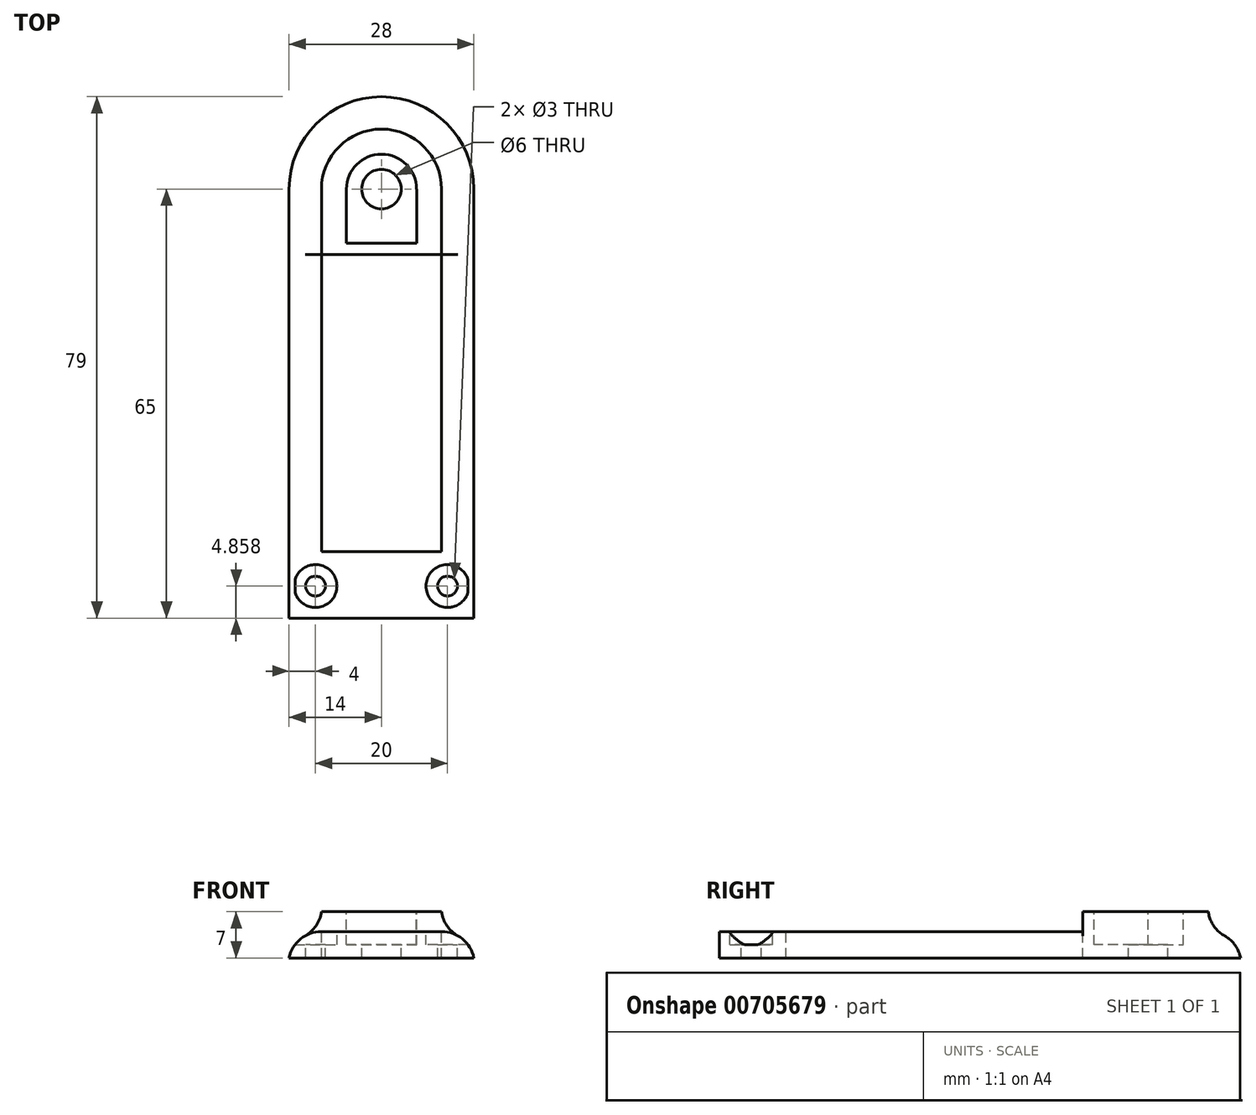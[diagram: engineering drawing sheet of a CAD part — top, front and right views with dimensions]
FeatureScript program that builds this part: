
annotation { "Feature Type Name" : "Feature", "Feature Type Description" : "" }
export const myFeature = defineFeature(function(context is Context, id is Id, definition is map)
    precondition{}
    {
        {
            var Q0;
            Q0=qCreatedBy(makeId("Top.planeOp"),FACE);
            var sketch = newSketch(context, id + "F0", { "sketchPlane" : qUnion([Q0])});
            skLineSegment(sketch, "E0.bottom", {"start": v(-14, 0) * mm, "end": v(14, 0) * mm});
            skLineSegment(sketch, "E0.top", {"start": v(-14, 65) * mm, "end": v(14, 65) * mm});
            skLineSegment(sketch, "E0.left", {"start": v(-14, 0) * mm, "end": v(-14, 65) * mm});
            skLineSegment(sketch, "E0.right", {"start": v(14, 0) * mm, "end": v(14, 65) * mm});
            skArc(sketch, "E1", {"start": v(14, 65) * mm, "mid": v(0, 79) * mm, "end": v(-14, 65) * mm});
            skSolve(sketch);
        }
        {
            var Q0;
            Q0=makeQuery(id+"F0.imprint","IMPRINT",FACE,{"disambiguationData":[TD([[makeQuery(id+"F0.imprint","IMPRINT",EDGE,{"derivedFrom":sQuery(id+"F0.wireOp",EDGE,"E0.bottom")}),1.0]])]});
            var Q1;
            Q1=makeQuery(id+"F0.imprint","IMPRINT",FACE,{"disambiguationData":[TD([[makeQuery(id+"F0.imprint","IMPRINT",EDGE,{"derivedFrom":sQuery(id+"F0.wireOp",EDGE,"E0.top")}),1.0]])]});
            extrude(context, id + "F1", {"entities" : qUnion([Q0, Q1]), "depth" : 4 * mm, "offsetDistance" : 25 * mm});
        }
        {
            var Q0;
            Q0=makeQuery(id+"F1.opExtrude","CAP_FACE",FACE,{"disambiguationData":[OSD([sQuery(id+"F0.wireOp",EDGE,"E0.bottom"),sQuery(id+"F0.wireOp",EDGE,"E0.left"),sQuery(id+"F0.wireOp",EDGE,"E0.right"),sQuery(id+"F0.wireOp",EDGE,"E1")])],"isStart":false});
            var sketch = newSketch(context, id + "F2", { "sketchPlane" : qUnion([Q0])});
            skCircle(sketch, "E2", {"center": v(-10, 4.86) * mm, "radius": 1.5 * mm});
            skSolve(sketch);
        }
        {
            var Q0;
            Q0=makeQuery(id+"F2.imprint","IMPRINT",FACE,{"disambiguationData":[TD([[makeQuery(id+"F2.imprint","IMPRINT",EDGE,{"derivedFrom":sQuery(id+"F2.wireOp",EDGE,"E2")}),1.0]])]});
            extrude(context, id + "F3", {"entities" : qUnion([Q0]), "operationType" : NewBodyOperationType.REMOVE, "oppositeDirection" : true, "depth" : 25 * mm, "offsetDistance" : 25 * mm});
        }
        {
            var Q0;
            Q0=makeQuery(id+"F1.opExtrude","CAP_FACE",FACE,{"disambiguationData":[OSD([sQuery(id+"F0.wireOp",EDGE,"E0.bottom"),sQuery(id+"F0.wireOp",EDGE,"E0.left"),sQuery(id+"F0.wireOp",EDGE,"E0.right"),sQuery(id+"F0.wireOp",EDGE,"E1")])],"isStart":false});
            var sketch = newSketch(context, id + "F4", { "sketchPlane" : qUnion([Q0])});
            skCircle(sketch, "E3", {"center": v(-10, 4.86) * mm, "radius": 3.25 * mm});
            skSolve(sketch);
        }
        {
            var Q0;
            Q0=makeQuery(id+"F4.imprint","IMPRINT",FACE,{"disambiguationData":[TD([[makeQuery(id+"F4.imprint","IMPRINT",EDGE,{"derivedFrom":sQuery(id+"F4.wireOp",EDGE,"E3")}),1.0]])]});
            extrude(context, id + "F5", {"entities" : qUnion([Q0]), "operationType" : NewBodyOperationType.REMOVE, "oppositeDirection" : true, "depth" : 2 * mm, "offsetDistance" : 25 * mm});
        }
        {
            var Q0;
            Q0=makeQuery(id+"F1.opExtrude","SWEPT_BODY",BODY,{"disambiguationData":[OSD([sQuery(id+"F0.wireOp",EDGE,"E0.bottom"),sQuery(id+"F0.wireOp",EDGE,"E0.left"),sQuery(id+"F0.wireOp",EDGE,"E0.right"),sQuery(id+"F0.wireOp",EDGE,"E1")])]});
            var Q1;
            Q1=qCreatedBy(makeId("Right.planeOp"),FACE);
            mirror(context, id + "F6", {"operationType" : NewBodyOperationType.INTERSECT, "entities" : qUnion([Q0]), "mirrorPlane" : qUnion([Q1])});
        }
        {
            var Q0;
            Q0=makeQuery(id+"F1.opExtrude","CAP_EDGE",EDGE,{"disambiguationData":[OSD([sQuery(id+"F0.wireOp",EDGE,"E0.left")])],"isStart":false});
            fillet(context, id + "F7", {"entities" : qUnion([Q0]), "radius" : 5 * mm, "tangentPropagation" : true, "allowEdgeOverflow" : false});
        }
        {
            var Q0;
            Q0=makeQuery(id+"F1.opExtrude","CAP_FACE",FACE,{"disambiguationData":[OSD([sQuery(id+"F0.wireOp",EDGE,"E0.bottom"),sQuery(id+"F0.wireOp",EDGE,"E0.left"),sQuery(id+"F0.wireOp",EDGE,"E0.right"),sQuery(id+"F0.wireOp",EDGE,"E1")])],"isStart":false});
            var sketch = newSketch(context, id + "F8", { "sketchPlane" : qUnion([Q0])});
            skLineSegment(sketch, "E4.bottom", {"start": v(-9.1, 10.1) * mm, "end": v(9.1, 10.1) * mm});
            skLineSegment(sketch, "E4.top", {"start": v(-9.1, 55.1) * mm, "end": v(9.1, 55.1) * mm});
            skLineSegment(sketch, "E4.left", {"start": v(-9.1, 10.1) * mm, "end": v(-9.1, 55.1) * mm});
            skLineSegment(sketch, "E4.right", {"start": v(9.1, 10.1) * mm, "end": v(9.1, 55.1) * mm});
            skSolve(sketch);
        }
        {
            var Q0;
            Q0=makeQuery(id+"F8.imprint","IMPRINT",FACE,{"disambiguationData":[TD([[makeQuery(id+"F8.imprint","IMPRINT",EDGE,{"derivedFrom":sQuery(id+"F8.wireOp",EDGE,"E4.bottom")}),1.0]])]});
            extrude(context, id + "F9", {"entities" : qUnion([Q0]), "operationType" : NewBodyOperationType.REMOVE, "oppositeDirection" : true, "depth" : 25 * mm, "offsetDistance" : 25 * mm});
        }
        {
            var Q0;
            {var subQ0=sQuery(id+"F0.wireOp",EDGE,"E1");var subQ1=sQuery(id+"F0.wireOp",EDGE,"E0.right");var subQ2=sQuery(id+"F0.wireOp",EDGE,"E0.left");Q0=makeQuery(id+"F9.boolean.opBoolean","SPLIT",FACE,{"disambiguationData":[TD([makeQuery(id+"F7.opFillet","BLEND_FACE",FACE,{"disambiguationData":[OSD([subQ0])]})])],"derivedFrom":makeQuery(id+"F1.opExtrude","CAP_FACE",FACE,{"disambiguationData":[OSD([sQuery(id+"F0.wireOp",EDGE,"E0.bottom"),subQ2,subQ1,subQ0])],"isStart":false})});}
            var sketch = newSketch(context, id + "F10", { "sketchPlane" : qUnion([Q0])});
            skCircle(sketch, "E5", {"center": v(0, 65) * mm, "radius": 5.3 * mm});
            skLineSegment(sketch, "E6.bottom", {"start": v(-5.3, 65) * mm, "end": v(5.37, 65) * mm});
            skLineSegment(sketch, "E6.top", {"start": v(-5.3, 56.8) * mm, "end": v(5.37, 56.8) * mm});
            skLineSegment(sketch, "E6.left", {"start": v(-5.3, 65) * mm, "end": v(-5.3, 56.8) * mm});
            skLineSegment(sketch, "E6.right", {"start": v(5.37, 65) * mm, "end": v(5.37, 56.8) * mm});
            skSolve(sketch);
        }
        {
            var Q0;
            {var subQ0=sQuery(id+"F10.wireOp",EDGE,"E6.bottom");var subQ1=sQuery(id+"F10.wireOp",EDGE,"E5");var subQ3=makeQuery(id+"F10.imprint","INTERSECT",VERTEX,{"derivedFrom":[subQ1,subQ0]});Q0=makeQuery(id+"F10.imprint","IMPRINT",FACE,{"disambiguationData":[TD([[makeQuery(id+"F10.imprint","IMPRINT",EDGE,{"disambiguationData":[TD([[subQ3,1.0]])],"derivedFrom":subQ1}),1.0]])]});}
            var Q1;
            {var subQ0=sQuery(id+"F10.wireOp",EDGE,"E6.bottom");var subQ1=sQuery(id+"F10.wireOp",EDGE,"E5");var subQ3=makeQuery(id+"F10.imprint","INTERSECT",VERTEX,{"derivedFrom":[subQ1,subQ0]});Q1=makeQuery(id+"F10.imprint","IMPRINT",FACE,{"disambiguationData":[TD([[makeQuery(id+"F10.imprint","IMPRINT",EDGE,{"disambiguationData":[TD([[subQ3,-1.0]])],"derivedFrom":subQ1}),1.0]])]});}
            var Q2;
            Q2=makeQuery(id+"F10.imprint","IMPRINT",FACE,{"disambiguationData":[TD([[makeQuery(id+"F10.imprint","IMPRINT",EDGE,{"derivedFrom":sQuery(id+"F10.wireOp",EDGE,"E6.top")}),1.0]])]});
            extrude(context, id + "F11", {"entities" : qUnion([Q0, Q1, Q2]), "operationType" : NewBodyOperationType.REMOVE, "oppositeDirection" : true, "depth" : 2 * mm, "offsetDistance" : 25 * mm});
        }
        {
            var Q0;
            {var subQ0=sQuery(id+"F0.wireOp",EDGE,"E1");var subQ1=sQuery(id+"F0.wireOp",EDGE,"E0.right");var subQ2=sQuery(id+"F0.wireOp",EDGE,"E0.left");Q0=makeQuery(id+"F9.boolean.opBoolean","SPLIT",FACE,{"disambiguationData":[TD([makeQuery(id+"F7.opFillet","BLEND_FACE",FACE,{"disambiguationData":[OSD([subQ0])]})])],"derivedFrom":makeQuery(id+"F1.opExtrude","CAP_FACE",FACE,{"disambiguationData":[OSD([sQuery(id+"F0.wireOp",EDGE,"E0.bottom"),subQ2,subQ1,subQ0])],"isStart":false})});}
            extrude(context, id + "F12", {"entities" : qUnion([Q0]), "operationType" : NewBodyOperationType.ADD, "depth" : 3 * mm, "offsetDistance" : 25 * mm});
        }
        {
            var Q0;
            Q0=makeQuery(id+"F11.boolean.opBoolean","COPY",FACE,{"derivedFrom":makeQuery(id+"F11.opExtrude","CAP_FACE",FACE,{"disambiguationData":[OSD([sQuery(id+"F10.wireOp",EDGE,"E5"),sQuery(id+"F10.wireOp",EDGE,"E6.bottom"),sQuery(id+"F10.wireOp",EDGE,"E6.top"),sQuery(id+"F10.wireOp",EDGE,"E6.left"),sQuery(id+"F10.wireOp",EDGE,"E6.right")])],"isStart":false})});
            var sketch = newSketch(context, id + "F13", { "sketchPlane" : qUnion([Q0])});
            skCircle(sketch, "E7", {"center": v(0, 65) * mm, "radius": 3 * mm});
            skSolve(sketch);
        }
        {
            var Q0;
            Q0=makeQuery(id+"F13.imprint","IMPRINT",FACE,{"disambiguationData":[TD([[makeQuery(id+"F13.imprint","IMPRINT",EDGE,{"derivedFrom":sQuery(id+"F13.wireOp",EDGE,"E7")}),1.0]])]});
            extrude(context, id + "F14", {"entities" : qUnion([Q0]), "operationType" : NewBodyOperationType.REMOVE, "oppositeDirection" : true, "depth" : 25 * mm, "offsetDistance" : 25 * mm});
        }
        {
            var Q0;
            {var subQ0=sQuery(id+"F0.wireOp",EDGE,"E1");var subQ1=sQuery(id+"F0.wireOp",EDGE,"E0.right");var subQ2=sQuery(id+"F0.wireOp",EDGE,"E0.left");var subQ3=sQuery(id+"F0.wireOp",EDGE,"E0.bottom");var subQ4=makeQuery(id+"F7.opFillet","BLEND_EDGE",EDGE,{"blendedFrom":[makeQuery(id+"F1.opExtrude","CAP_EDGE",EDGE,{"disambiguationData":[OSD([subQ0])],"isStart":false}),makeQuery(id+"F1.opExtrude","CAP_FACE",FACE,{"disambiguationData":[OSD([subQ3,subQ2,subQ1,subQ0])],"isStart":false})],"blendedInto":[makeQuery(id+"F1.opExtrude","CAP_FACE",FACE,{"disambiguationData":[OSD([subQ3,subQ2,subQ1,subQ0])],"isStart":false})]});Q0=makeQuery(id+"F12.boolean.opBoolean","MERGE",EDGE,{"derivedFrom":[subQ4,makeQuery(id+"F12.opExtrude","CAP_EDGE",EDGE,{"disambiguationData":[OSD([subQ3,subQ2,subQ1,subQ0]),TDD([subQ4])],"isStart":true})]});}
            fillet(context, id + "F15", {"entities" : qUnion([Q0]), "radius" : 5 * mm, "tangentPropagation" : true, "allowEdgeOverflow" : false});
        }
    });
